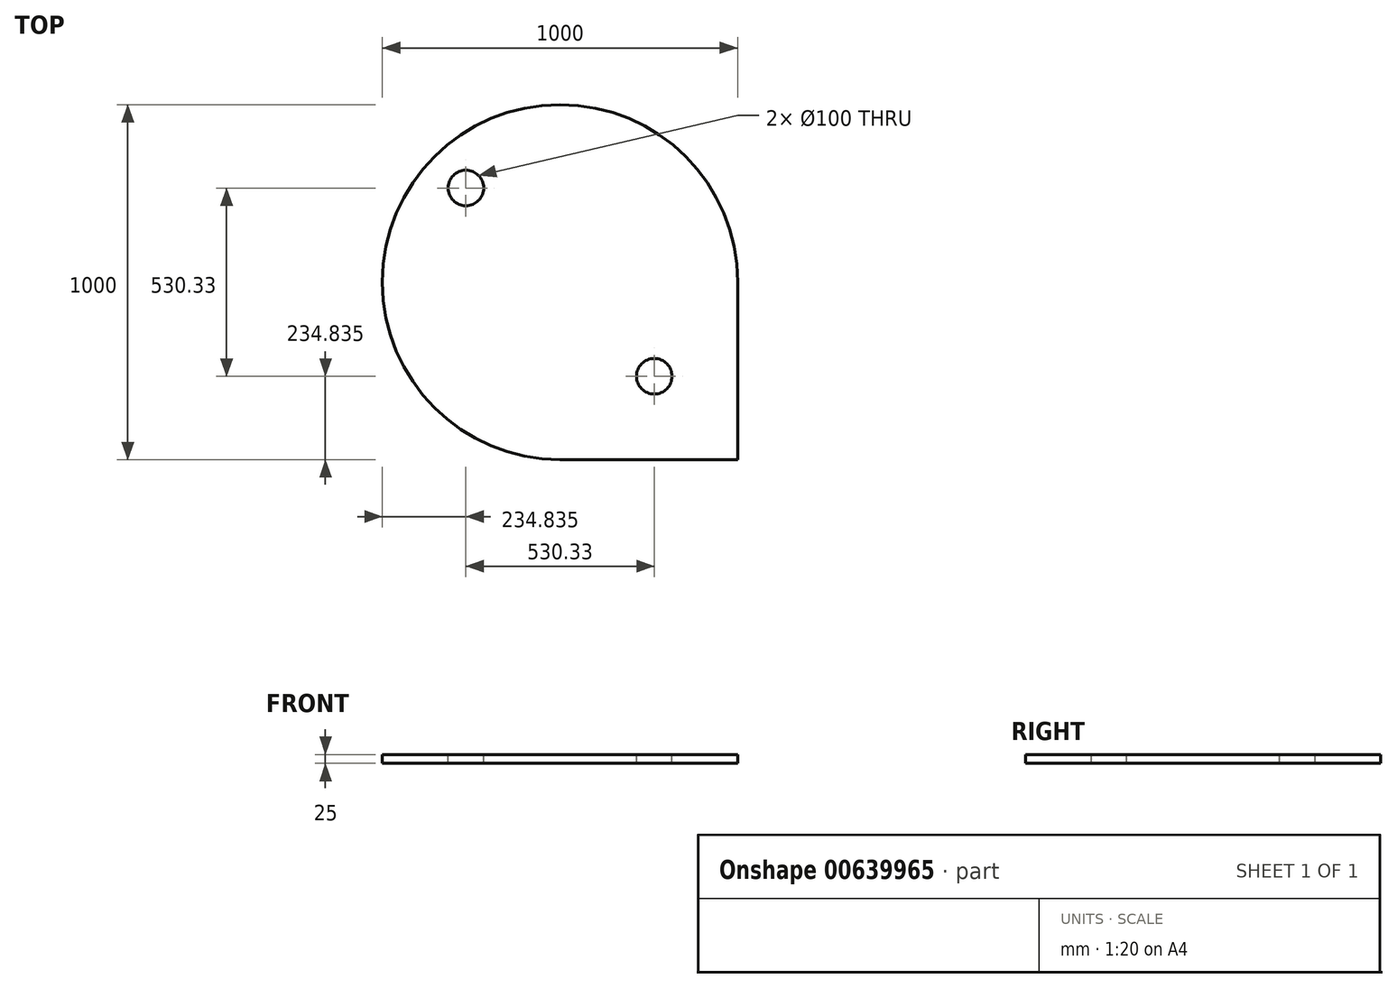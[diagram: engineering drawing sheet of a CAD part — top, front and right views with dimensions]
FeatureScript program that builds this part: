
annotation { "Feature Type Name" : "Feature", "Feature Type Description" : "" }
export const myFeature = defineFeature(function(context is Context, id is Id, definition is map)
    precondition{}
    {
        {
            var Q0;
            Q0=qCreatedBy(makeId("Top.planeOp"),FACE);
            var sketch = newSketch(context, id + "F0", { "sketchPlane" : qUnion([Q0])});
            skArc(sketch, "E0", {"start": v(500, 0) * mm, "mid": v(-353.55, 353.55) * mm, "end": v(0, -500) * mm});
            skLineSegment(sketch, "E1", {"start": v(0, -500) * mm, "end": v(500, -500) * mm});
            skLineSegment(sketch, "E2", {"start": v(500, 0) * mm, "end": v(500, -500) * mm});
            skSolve(sketch);
        }
        {
            var Q0;
            Q0=makeQuery(id+"F0.imprint","IMPRINT",FACE,{"disambiguationData":[TD([[makeQuery(id+"F0.imprint","IMPRINT",EDGE,{"derivedFrom":sQuery(id+"F0.wireOp",EDGE,"E0")}),1.0]])]});
            var Q1;
            Q1 = qSketchRegion(id + "F0", true);
            extrude(context, id + "F1", {"entities" : qUnion([Q0, Q1]), "depth" : 25 * mm, "offsetDistance" : 25 * mm});
        }
        {
            var Q0;
            Q0=makeQuery(id+"F1.opExtrude","CAP_FACE",FACE,{"disambiguationData":[OSD([sQuery(id+"F0.wireOp",EDGE,"E0"),sQuery(id+"F0.wireOp",EDGE,"E1"),sQuery(id+"F0.wireOp",EDGE,"E2")])],"isStart":false});
            var sketch = newSketch(context, id + "F2", { "sketchPlane" : qUnion([Q0])});
            skCircle(sketch, "E3", {"center": v(265.17, -265.17) * mm, "radius": 50 * mm});
            skCircle(sketch, "E4", {"center": v(-265.17, 265.17) * mm, "radius": 50 * mm});
            skLineSegment(sketch, "E5", {"start": v(0, 0) * mm, "end": v(-265.17, 265.17) * mm});
            skLineSegment(sketch, "E6", {"start": v(0, 0) * mm, "end": v(0, 403.33) * mm});
            skSolve(sketch);
        }
        {
            var Q0;
            Q0=makeQuery(id+"F2.imprint","IMPRINT",FACE,{"disambiguationData":[TD([[makeQuery(id+"F2.imprint","IMPRINT",EDGE,{"derivedFrom":sQuery(id+"F2.wireOp",EDGE,"E4")}),1.0]])]});
            var Q1;
            Q1=makeQuery(id+"F2.imprint","IMPRINT",FACE,{"disambiguationData":[TD([[makeQuery(id+"F2.imprint","IMPRINT",EDGE,{"derivedFrom":sQuery(id+"F2.wireOp",EDGE,"E3")}),1.0]])]});
            extrude(context, id + "F3", {"entities" : qUnion([Q0, Q1]), "operationType" : NewBodyOperationType.REMOVE, "endBound" : BoundingType.UP_TO_NEXT, "oppositeDirection" : true, "depth" : 25 * mm, "offsetDistance" : 25 * mm});
        }
    });
